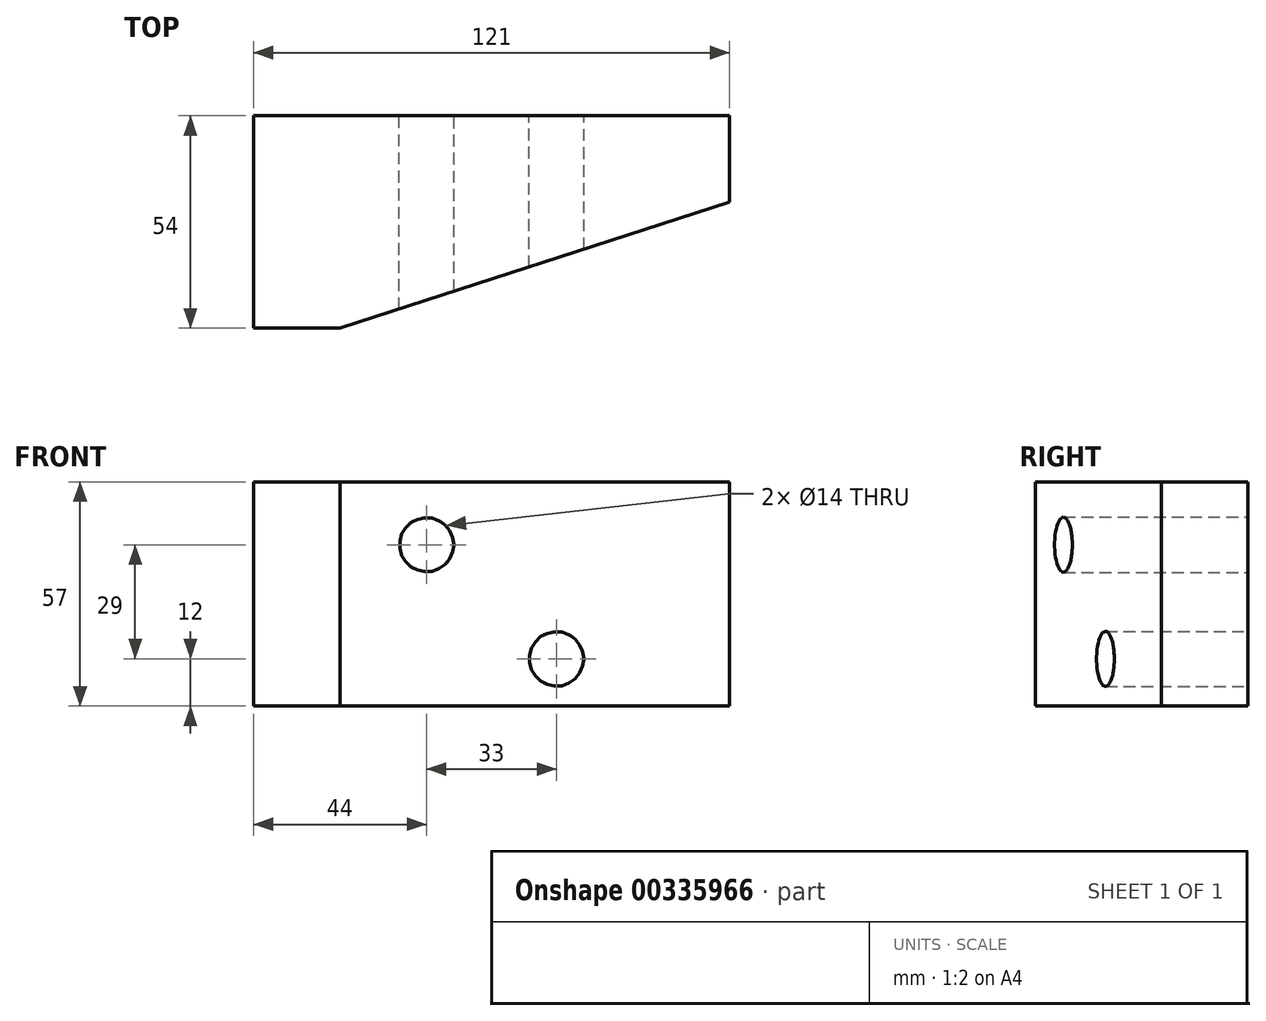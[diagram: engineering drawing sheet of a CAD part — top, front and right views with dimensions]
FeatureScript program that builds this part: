
annotation { "Feature Type Name" : "Feature", "Feature Type Description" : "" }
export const myFeature = defineFeature(function(context is Context, id is Id, definition is map)
    precondition{}
    {
        {
            var Q0;
            Q0=qCreatedBy(makeId("Front.planeOp"),FACE);
            var sketch = newSketch(context, id + "F0", { "sketchPlane" : qUnion([Q0])});
            skLineSegment(sketch, "E0", {"start": v(0, 57) * mm, "end": v(0, 0) * mm});
            skLineSegment(sketch, "E1", {"start": v(0, 0) * mm, "end": v(121, 0) * mm});
            skLineSegment(sketch, "E2", {"start": v(121, 0) * mm, "end": v(121, 57) * mm});
            skLineSegment(sketch, "E3", {"start": v(121, 57) * mm, "end": v(0, 57) * mm});
            skLineSegment(sketch, "E4", {"start": v(62, 57) * mm, "end": v(121, 11) * mm});
            skCircle(sketch, "E5", {"center": v(44, 41) * mm, "radius": 7 * mm});
            skCircle(sketch, "E6", {"center": v(77, 12) * mm, "radius": 7 * mm});
            skLineSegment(sketch, "E7", {"start": v(0, 0) * mm, "end": v(0, 46) * mm});
            skLineSegment(sketch, "E8", {"start": v(0, 46) * mm, "end": v(62, 0) * mm});
            skLineSegment(sketch, "E9", {"start": v(62, 0) * mm, "end": v(0, 0) * mm});
            skLineSegment(sketch, "E10", {"start": v(22, 0) * mm, "end": v(22, 29.68) * mm});
            skSolve(sketch);
        }
        {
            var Q0;
            Q0 = qSketchRegion(id + "F0", true);
            extrude(context, id + "F1", {"entities" : qUnion([Q0]), "depth" : 54 * mm});
        }
        {
            var Q0;
            Q0=makeQuery(id+"F1.opExtrude","SWEPT_FACE",FACE,{"disambiguationData":[OSD([sQuery(id+"F0.wireOp",EDGE,"E3")])]});
            var sketch = newSketch(context, id + "F2", { "sketchPlane" : qUnion([Q0])});
            skLineSegment(sketch, "E11", {"start": v(22, -54) * mm, "end": v(121, -22) * mm});
            skLineSegment(sketch, "E12", {"start": v(121, -22) * mm, "end": v(121, 0) * mm});
            skLineSegment(sketch, "E13", {"start": v(121, 0) * mm, "end": v(0, 0) * mm});
            skLineSegment(sketch, "E14", {"start": v(0, 0) * mm, "end": v(0, -54) * mm});
            skLineSegment(sketch, "E15", {"start": v(0, -54) * mm, "end": v(22, -54) * mm});
            skLineSegment(sketch, "E16", {"start": v(22, -54) * mm, "end": v(121, -54) * mm});
            skLineSegment(sketch, "E17", {"start": v(121, -54) * mm, "end": v(121, -22) * mm});
            skSolve(sketch);
        }
        {
            var Q0;
            Q0=makeQuery(id+"F2.imprint","IMPRINT",FACE,{"disambiguationData":[TD([[makeQuery(id+"F2.imprint","IMPRINT",EDGE,{"derivedFrom":sQuery(id+"F2.wireOp",EDGE,"E11")}),-1.0]])]});
            extrude(context, id + "F3", {"entities" : qUnion([Q0]), "operationType" : NewBodyOperationType.REMOVE, "endBound" : BoundingType.THROUGH_ALL, "oppositeDirection" : true, "depth" : 25 * mm});
        }
    });
